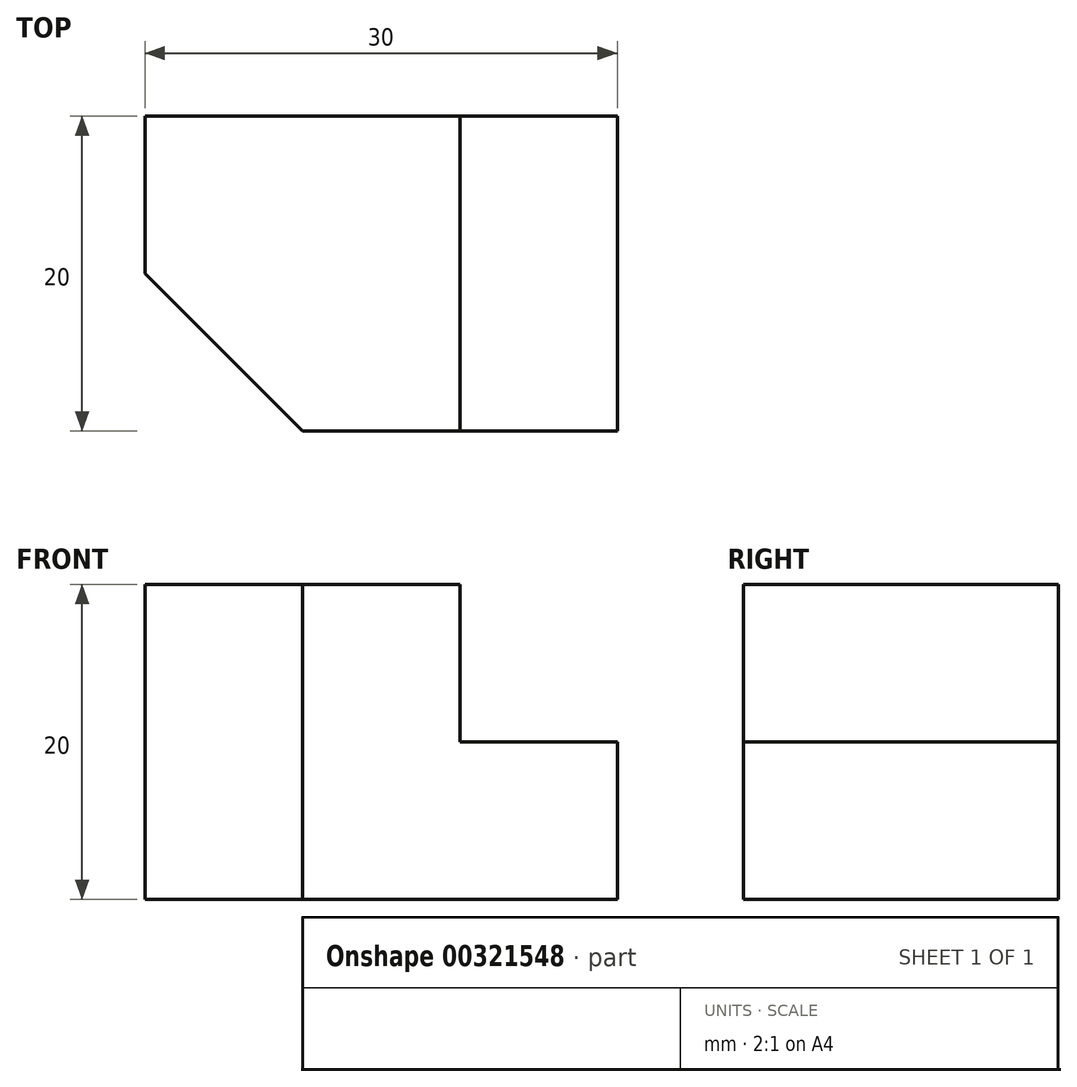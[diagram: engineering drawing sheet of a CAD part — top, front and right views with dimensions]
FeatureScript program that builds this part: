
annotation { "Feature Type Name" : "Feature", "Feature Type Description" : "" }
export const myFeature = defineFeature(function(context is Context, id is Id, definition is map)
    precondition{}
    {
        {
            var Q0;
            Q0=qCreatedBy(makeId("Top.planeOp"),FACE);
            var sketch = newSketch(context, id + "F0", { "sketchPlane" : qUnion([Q0])});
            skLineSegment(sketch, "E0", {"start": v(0, 0) * mm, "end": v(0, -10) * mm});
            skLineSegment(sketch, "E1", {"start": v(0, -10) * mm, "end": v(10, -20) * mm});
            skLineSegment(sketch, "E2", {"start": v(10, -20) * mm, "end": v(30, -20) * mm});
            skLineSegment(sketch, "E3", {"start": v(30, -20) * mm, "end": v(30, 0) * mm});
            skLineSegment(sketch, "E4", {"start": v(30, 0) * mm, "end": v(0, 0) * mm});
            skSolve(sketch);
        }
        {
            var Q0;
            Q0=makeQuery(id+"F0.imprint","IMPRINT",FACE,{"disambiguationData":[TD([[makeQuery(id+"F0.imprint","IMPRINT",EDGE,{"derivedFrom":sQuery(id+"F0.wireOp",EDGE,"E0")}),1.0]])]});
            extrude(context, id + "F1", {"entities" : qUnion([Q0]), "depth" : 20 * mm});
        }
        {
            var Q0;
            Q0=makeQuery(id+"F1.opExtrude","CAP_FACE",FACE,{"disambiguationData":[OSD([sQuery(id+"F0.wireOp",EDGE,"E0"),sQuery(id+"F0.wireOp",EDGE,"E1"),sQuery(id+"F0.wireOp",EDGE,"E2"),sQuery(id+"F0.wireOp",EDGE,"E3"),sQuery(id+"F0.wireOp",EDGE,"E4")])],"isStart":false});
            var sketch = newSketch(context, id + "F2", { "sketchPlane" : qUnion([Q0])});
            skLineSegment(sketch, "E5.bottom", {"start": v(30, 0) * mm, "end": v(20, 0) * mm});
            skLineSegment(sketch, "E5.top", {"start": v(30, -20) * mm, "end": v(20, -20) * mm});
            skLineSegment(sketch, "E5.left", {"start": v(30, 0) * mm, "end": v(30, -20) * mm});
            skLineSegment(sketch, "E5.right", {"start": v(20, 0) * mm, "end": v(20, -20) * mm});
            skSolve(sketch);
        }
        {
            var Q0;
            Q0=makeQuery(id+"F2.imprint","IMPRINT",FACE,{"disambiguationData":[TD([[makeQuery(id+"F2.imprint","IMPRINT",EDGE,{"derivedFrom":sQuery(id+"F2.wireOp",EDGE,"E5.bottom")}),1.0]])]});
            extrude(context, id + "F3", {"entities" : qUnion([Q0]), "operationType" : NewBodyOperationType.REMOVE, "oppositeDirection" : true, "depth" : 10 * mm});
        }
    });
